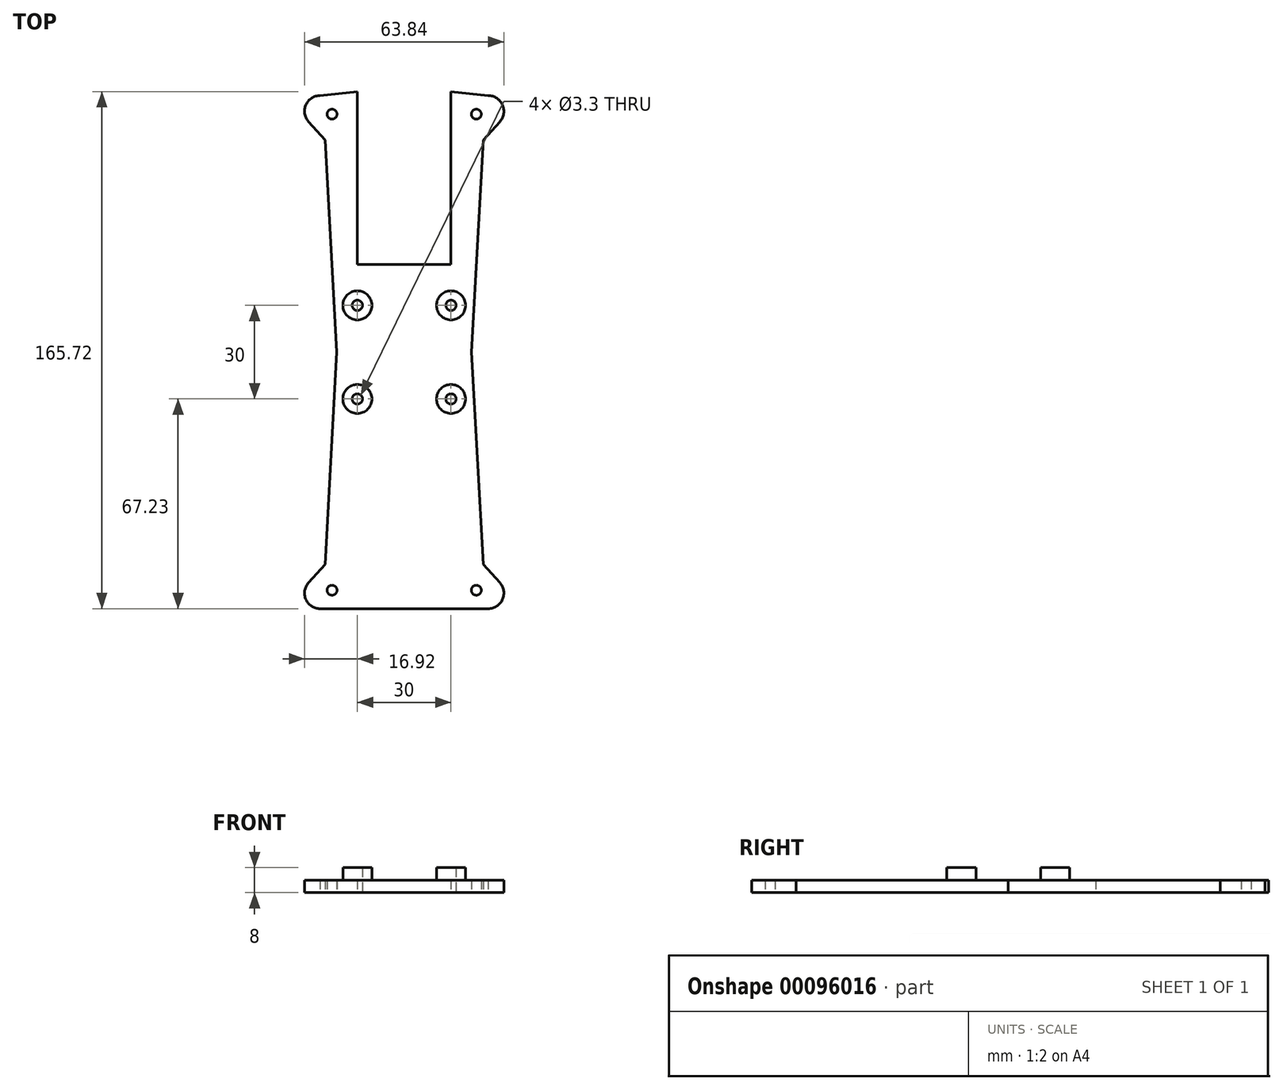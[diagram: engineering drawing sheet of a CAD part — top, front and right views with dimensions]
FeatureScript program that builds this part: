
annotation { "Feature Type Name" : "Feature", "Feature Type Description" : "" }
export const myFeature = defineFeature(function(context is Context, id is Id, definition is map)
    precondition{}
    {
        {
            var Q0;
            Q0=qCreatedBy(makeId("Top.planeOp"),FACE);
            var sketch = newSketch(context, id + "F0", { "sketchPlane" : qUnion([Q0])});
            skLineSegment(sketch, "E0.0", {"start": v(-36, -55.08) * mm, "end": v(-36, 0) * mm, "construction": true});
            skCircle(sketch, "E1", {"center": v(-23.1, -76.3) * mm, "radius": 1.6 * mm});
            skLineSegment(sketch, "E2", {"start": v(-21.57, 0) * mm, "end": v(-25.3, -67.98) * mm});
            skPoint(sketch, "E3.middle", {"position": v(0, 0) * mm});
            skCircle(sketch, "E4", {"center": v(-15, -15) * mm, "radius": 1.65 * mm});
            skLineSegment(sketch, "E5", {"start": v(-25.3, -67.98) * mm, "end": v(-30.63, -73.88) * mm});
            skLineSegment(sketch, "E6", {"start": v(-26.92, -82.23) * mm, "end": v(0, -82.23) * mm});
            skPoint(sketch, "E7.visualSharp", {"position": v(-38.18, -82.23) * mm});
            skArc(sketch, "E7.filletArc", {"start": v(-30.63, -73.88) * mm, "mid": v(-31.5, -79.26) * mm, "end": v(-26.92, -82.23) * mm});
            skArc(sketch, "E8.MirrorCS", {"start": v(30.63, -73.88) * mm, "mid": v(31.5, -79.26) * mm, "end": v(26.92, -82.23) * mm});
            skCircle(sketch, "E9.MirrorC", {"center": v(23.1, -76.3) * mm, "radius": 1.6 * mm});
            skCircle(sketch, "E10.MirrorC", {"center": v(15, -15) * mm, "radius": 1.65 * mm});
            skLineSegment(sketch, "E11.MirrorCS", {"start": v(26.92, -82.23) * mm, "end": v(0, -82.23) * mm});
            skPoint(sketch, "E12.MirrorP", {"position": v(38.18, -82.23) * mm});
            skLineSegment(sketch, "E13.MirrorCS", {"start": v(25.3, -67.98) * mm, "end": v(30.63, -73.88) * mm});
            skLineSegment(sketch, "E14.MirrorCS", {"start": v(36, -55.08) * mm, "end": v(36, 0) * mm, "construction": true});
            skLineSegment(sketch, "E15.MirrorCS", {"start": v(21.57, 0) * mm, "end": v(25.3, -67.98) * mm});
            skCircle(sketch, "E16.MirrorC", {"center": v(15, 15) * mm, "radius": 1.65 * mm});
            skArc(sketch, "E17.MirrorCS", {"start": v(30.63, 73.88) * mm, "mid": v(31.5, 79.26) * mm, "end": v(26.92, 82.23) * mm});
            skCircle(sketch, "E18.MirrorC", {"center": v(-15, 15) * mm, "radius": 1.65 * mm});
            skCircle(sketch, "E19.MirrorC", {"center": v(-23.1, 76.3) * mm, "radius": 1.6 * mm});
            skCircle(sketch, "E20.MirrorC", {"center": v(23.1, 76.3) * mm, "radius": 1.6 * mm});
            skArc(sketch, "E21.MirrorCS", {"start": v(-30.63, 73.88) * mm, "mid": v(-31.5, 79.26) * mm, "end": v(-26.92, 82.23) * mm});
            skLineSegment(sketch, "E22.MirrorCS", {"start": v(21.57, 0) * mm, "end": v(25.3, 67.98) * mm});
            skLineSegment(sketch, "E23.MirrorCS", {"start": v(-36, 55.08) * mm, "end": v(-36, 0) * mm, "construction": true});
            skLineSegment(sketch, "E24.MirrorCS", {"start": v(-21.57, 0) * mm, "end": v(-25.3, 67.98) * mm});
            skLineSegment(sketch, "E25.MirrorCS", {"start": v(25.3, 67.98) * mm, "end": v(30.63, 73.88) * mm});
            skPoint(sketch, "E26.MirrorP", {"position": v(-38.18, 82.23) * mm});
            skLineSegment(sketch, "E27.MirrorCS", {"start": v(-25.3, 67.98) * mm, "end": v(-30.63, 73.88) * mm});
            skPoint(sketch, "E28.MirrorP", {"position": v(38.18, 82.23) * mm});
            skLineSegment(sketch, "E29.MirrorCS", {"start": v(36, 55.08) * mm, "end": v(36, 0) * mm, "construction": true});
            skPoint(sketch, "E30.oppositeSnap0", {"position": v(-15, 83.49) * mm});
            skLineSegment(sketch, "E30.top", {"start": v(-15, 28.12) * mm, "end": v(-15, 28.12) * mm});
            skLineSegment(sketch, "E31.bottom", {"start": v(-15, 28.12) * mm, "end": v(0, 28.12) * mm});
            skLineSegment(sketch, "E31.top", {"start": v(-15, 28.12) * mm, "end": v(0, 28.12) * mm});
            skLineSegment(sketch, "E31.right", {"start": v(0, 28.12) * mm, "end": v(0, 28.12) * mm});
            skLineSegment(sketch, "E32.MirrorCS", {"start": v(15, 28.12) * mm, "end": v(0, 28.12) * mm});
            skLineSegment(sketch, "E33.MirrorCS", {"start": v(15, 28.12) * mm, "end": v(15, 28.12) * mm});
            skLineSegment(sketch, "E34", {"start": v(-15, 83.49) * mm, "end": v(-26.92, 82.23) * mm});
            skLineSegment(sketch, "E35.MirrorCS", {"start": v(15, 83.49) * mm, "end": v(26.92, 82.23) * mm});
            skLineSegment(sketch, "E36", {"start": v(-15, 28.12) * mm, "end": v(-15, 83.49) * mm});
            skLineSegment(sketch, "E37.MirrorCS", {"start": v(15, 28.12) * mm, "end": v(15, 83.49) * mm});
            skSolve(sketch);
        }
        {
            var Q0;
            Q0 = qSketchRegion(id + "F0", true);
            extrude(context, id + "F1", {"entities" : qUnion([Q0]), "depth" : 4 * mm});
        }
        {
            var Q0;
            Q0=qCreatedBy(makeId("Top.planeOp"),FACE);
            var sketch = newSketch(context, id + "F2", { "sketchPlane" : qUnion([Q0])});
            skCircle(sketch, "E38.0", {"center": v(-15, 15) * mm, "radius": 1.65 * mm});
            skCircle(sketch, "E39.0", {"center": v(15, 15) * mm, "radius": 1.65 * mm});
            skCircle(sketch, "E40.0", {"center": v(15, -15) * mm, "radius": 1.65 * mm});
            skCircle(sketch, "E41.0", {"center": v(-15, -15) * mm, "radius": 1.65 * mm});
            skCircle(sketch, "E42.0", {"center": v(-15, 15) * mm, "radius": 4.65 * mm});
            skCircle(sketch, "E43.MirrorC", {"center": v(-15, -15) * mm, "radius": 4.65 * mm});
            skCircle(sketch, "E44.MirrorC", {"center": v(15, 15) * mm, "radius": 4.65 * mm});
            skCircle(sketch, "E45.MirrorC", {"center": v(15, -15) * mm, "radius": 4.65 * mm});
            skSolve(sketch);
        }
        {
            var Q0;
            Q0 = qSketchRegion(id + "F2", true);
            extrude(context, id + "F3", {"entities" : qUnion([Q0]), "operationType" : NewBodyOperationType.ADD, "depth" : 8 * mm});
        }
    });
